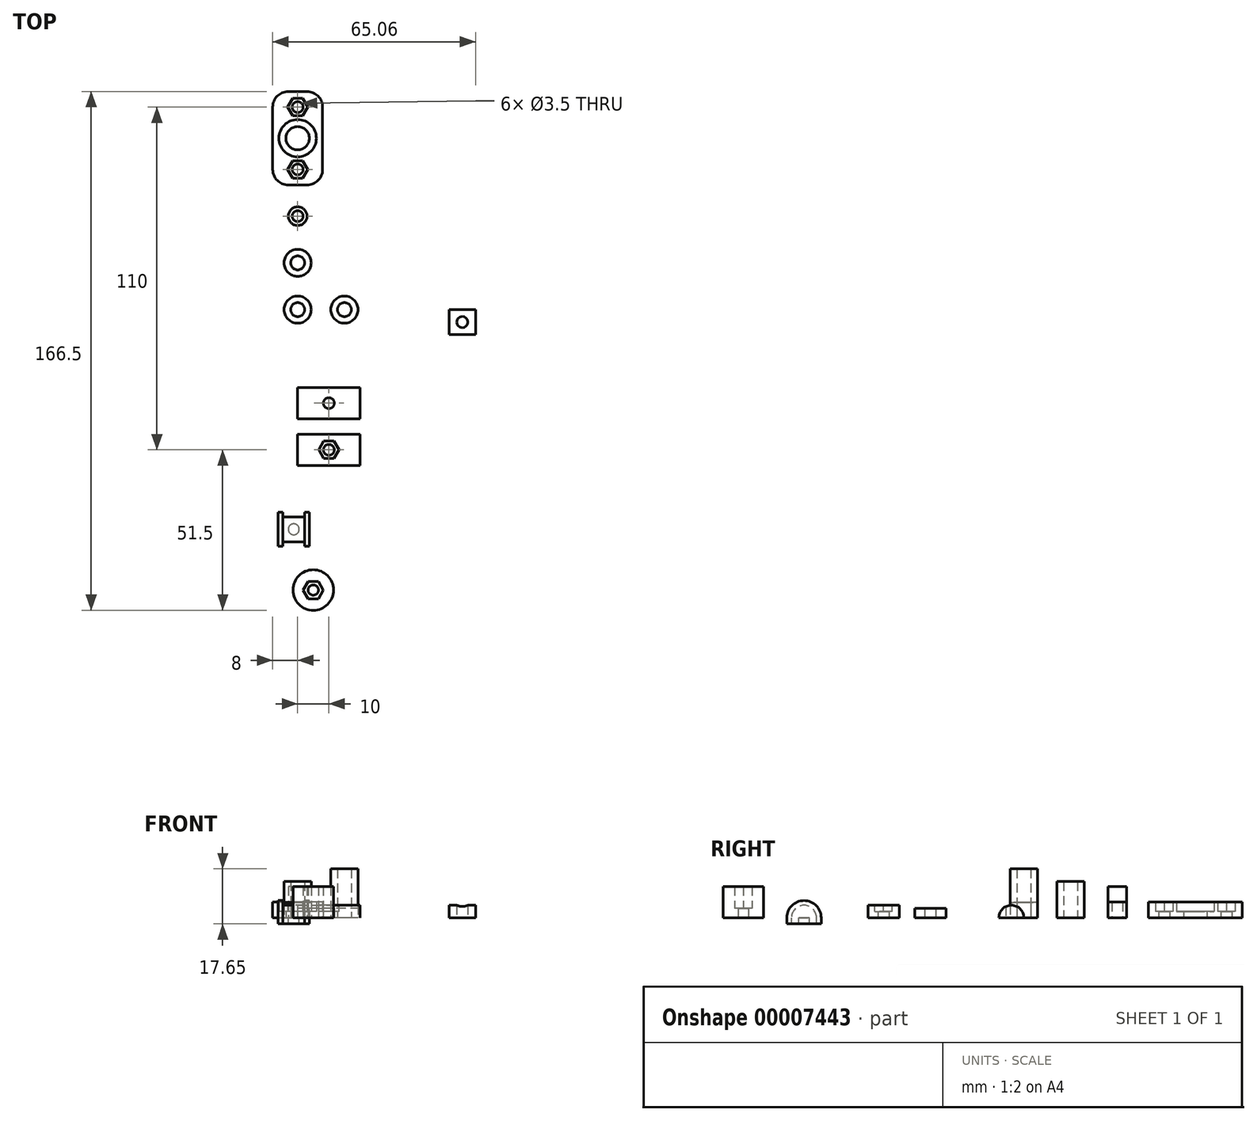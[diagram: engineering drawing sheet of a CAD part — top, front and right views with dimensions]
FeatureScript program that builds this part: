
annotation { "Feature Type Name" : "Feature", "Feature Type Description" : "" }
export const myFeature = defineFeature(function(context is Context, id is Id, definition is map)
    precondition{}
    {
        {
            var Q0;
            Q0=qCreatedBy(makeId("Top.planeOp"),FACE);
            var sketch = newSketch(context, id + "F0", { "sketchPlane" : qUnion([Q0])});
            skCircle(sketch, "E0", {"center": v(10, 30) * mm, "radius": 4.35 * mm});
            skCircle(sketch, "E1", {"center": v(10, 30) * mm, "radius": 2.25 * mm});
            skLineSegment(sketch, "E2.rect.bottom", {"start": v(30, -20) * mm, "end": v(10, -20) * mm});
            skLineSegment(sketch, "E2.rect.top", {"start": v(30, -10) * mm, "end": v(10, -10) * mm});
            skLineSegment(sketch, "E2.rect.left", {"start": v(30, -20) * mm, "end": v(30, -10) * mm});
            skLineSegment(sketch, "E2.rect.right", {"start": v(10, -20) * mm, "end": v(10, -10) * mm});
            skPoint(sketch, "E2.rect.middle", {"position": v(20, -15) * mm});
            skCircle(sketch, "E3", {"center": v(20, -15) * mm, "radius": 1.75 * mm});
            skLineSegment(sketch, "E4", {"start": v(10, -20) * mm, "end": v(10, -25) * mm, "construction": true});
            skLineSegment(sketch, "E5.rect.bottom", {"start": v(10, -25) * mm, "end": v(30, -25) * mm});
            skLineSegment(sketch, "E5.rect.top", {"start": v(10, -35) * mm, "end": v(30, -35) * mm});
            skLineSegment(sketch, "E5.rect.left", {"start": v(10, -25) * mm, "end": v(10, -35) * mm});
            skLineSegment(sketch, "E5.rect.right", {"start": v(30, -25) * mm, "end": v(30, -35) * mm});
            skPoint(sketch, "E5.rect.middle", {"position": v(20, -30) * mm});
            skLineSegment(sketch, "E6", {"start": v(30, -25) * mm, "end": v(30, -20) * mm, "construction": true});
            skCircle(sketch, "E7", {"center": v(20, -30) * mm, "radius": 1.75 * mm});
            skLineSegment(sketch, "E8", {"start": v(13.75, -55.5) * mm, "end": v(20.06, -55.5) * mm, "construction": true});
            skLineSegment(sketch, "E9", {"start": v(13.75, -55.5) * mm, "end": v(13.75, -50) * mm});
            skLineSegment(sketch, "E10", {"start": v(13.75, -50) * mm, "end": v(12.25, -50) * mm});
            skLineSegment(sketch, "E11", {"start": v(12.25, -50) * mm, "end": v(12.25, -51.5) * mm});
            skLineSegment(sketch, "E12", {"start": v(12.25, -51.5) * mm, "end": v(5.25, -51.5) * mm});
            skLineSegment(sketch, "E13", {"start": v(5.25, -51.5) * mm, "end": v(5.25, -50) * mm});
            skLineSegment(sketch, "E14", {"start": v(5.25, -50) * mm, "end": v(3.75, -50) * mm});
            skLineSegment(sketch, "E15", {"start": v(3.75, -50) * mm, "end": v(3.75, -55.5) * mm});
            skLineSegment(sketch, "E16", {"start": v(5.25, -50) * mm, "end": v(12.25, -50) * mm, "construction": true});
            skLineSegment(sketch, "E17.0.MirrorCS", {"start": v(3.75, -61) * mm, "end": v(3.75, -55.5) * mm});
            skLineSegment(sketch, "E17.1.MirrorCS", {"start": v(5.25, -61) * mm, "end": v(3.75, -61) * mm});
            skLineSegment(sketch, "E17.2.MirrorCS", {"start": v(5.25, -59.5) * mm, "end": v(5.25, -61) * mm});
            skLineSegment(sketch, "E17.3.MirrorCS", {"start": v(12.25, -59.5) * mm, "end": v(5.25, -59.5) * mm});
            skLineSegment(sketch, "E17.4.MirrorCS", {"start": v(12.25, -61) * mm, "end": v(12.25, -59.5) * mm});
            skLineSegment(sketch, "E17.5.MirrorCS", {"start": v(13.75, -55.5) * mm, "end": v(13.75, -61) * mm});
            skLineSegment(sketch, "E17.6.MirrorCS", {"start": v(13.75, -61) * mm, "end": v(12.25, -61) * mm});
            skLineSegment(sketch, "E18", {"start": v(3.75, -55.5) * mm, "end": v(13.75, -55.5) * mm});
            skCircle(sketch, "E19", {"center": v(8.75, -55.5) * mm, "radius": 1.75 * mm});
            skCircle(sketch, "E20", {"center": v(10, 15) * mm, "radius": 4.35 * mm});
            skCircle(sketch, "E21", {"center": v(10, 15) * mm, "radius": 2.25 * mm});
            skCircle(sketch, "E22", {"center": v(25, 15) * mm, "radius": 2.25 * mm});
            skCircle(sketch, "E23", {"center": v(25, 15) * mm, "radius": 4.35 * mm});
            skCircle(sketch, "E24", {"center": v(15, -75) * mm, "radius": 6.5 * mm});
            skCircle(sketch, "E25", {"center": v(15, -75) * mm, "radius": 1.65 * mm});
            skCircle(sketch, "E26.cCircle", {"center": v(15, -75) * mm, "radius": 2.8 * mm, "construction": true});
            skLineSegment(sketch, "E26.0", {"start": v(13.38, -72.2) * mm, "end": v(16.62, -72.2) * mm});
            skLineSegment(sketch, "E26.1", {"start": v(16.62, -72.2) * mm, "end": v(18.23, -75) * mm});
            skLineSegment(sketch, "E26.2", {"start": v(18.23, -75) * mm, "end": v(16.62, -77.8) * mm});
            skLineSegment(sketch, "E26.3", {"start": v(16.62, -77.8) * mm, "end": v(13.38, -77.8) * mm});
            skLineSegment(sketch, "E26.4", {"start": v(13.38, -77.8) * mm, "end": v(11.77, -75) * mm});
            skLineSegment(sketch, "E26.5", {"start": v(11.77, -75) * mm, "end": v(13.38, -72.2) * mm});
            skPoint(sketch, "E26.0.midPoint", {"position": v(15, -72.2) * mm});
            skLineSegment(sketch, "E27", {"start": v(10, 15) * mm, "end": v(25, 15) * mm, "construction": true});
            skLineSegment(sketch, "E28", {"start": v(10, 15) * mm, "end": v(10, 30) * mm, "construction": true});
            skLineSegment(sketch, "E29", {"start": v(10, 30) * mm, "end": v(10, 45) * mm, "construction": true});
            skCircle(sketch, "E30", {"center": v(10, 45) * mm, "radius": 1.75 * mm});
            skCircle(sketch, "E31", {"center": v(10, 45) * mm, "radius": 3 * mm});
            skLineSegment(sketch, "E32", {"start": v(10, 45) * mm, "end": v(10, 60) * mm, "construction": true});
            skLineSegment(sketch, "E33", {"start": v(10, 60) * mm, "end": v(10, 80) * mm, "construction": true});
            skLineSegment(sketch, "E34.rect.bottom", {"start": v(13, 55) * mm, "end": v(7, 55) * mm});
            skLineSegment(sketch, "E34.rect.top", {"start": v(13, 85) * mm, "end": v(7, 85) * mm});
            skLineSegment(sketch, "E34.rect.left", {"start": v(18, 60) * mm, "end": v(18, 80) * mm});
            skLineSegment(sketch, "E34.rect.right", {"start": v(2, 60) * mm, "end": v(2, 80) * mm});
            skPoint(sketch, "E34.rect.middle", {"position": v(10, 70) * mm});
            skCircle(sketch, "E35", {"center": v(10, 70) * mm, "radius": 3.75 * mm});
            skCircle(sketch, "E36", {"center": v(10, 60) * mm, "radius": 1.75 * mm});
            skCircle(sketch, "E37", {"center": v(10, 80) * mm, "radius": 1.75 * mm});
            skCircle(sketch, "E38.cCircle", {"center": v(10, 60) * mm, "radius": 2.8 * mm, "construction": true});
            skLineSegment(sketch, "E38.0", {"start": v(8.38, 62.8) * mm, "end": v(11.62, 62.8) * mm});
            skLineSegment(sketch, "E38.1", {"start": v(11.62, 62.8) * mm, "end": v(13.23, 60) * mm});
            skLineSegment(sketch, "E38.2", {"start": v(13.23, 60) * mm, "end": v(11.62, 57.2) * mm});
            skLineSegment(sketch, "E38.3", {"start": v(11.62, 57.2) * mm, "end": v(8.38, 57.2) * mm});
            skLineSegment(sketch, "E38.4", {"start": v(8.38, 57.2) * mm, "end": v(6.77, 60) * mm});
            skLineSegment(sketch, "E38.5", {"start": v(6.77, 60) * mm, "end": v(8.38, 62.8) * mm});
            skPoint(sketch, "E38.0.midPoint", {"position": v(10, 62.8) * mm});
            skCircle(sketch, "E39.cCircle", {"center": v(10, 80) * mm, "radius": 2.8 * mm, "construction": true});
            skLineSegment(sketch, "E39.0", {"start": v(8.38, 82.8) * mm, "end": v(11.62, 82.8) * mm});
            skLineSegment(sketch, "E39.1", {"start": v(11.62, 82.8) * mm, "end": v(13.23, 80) * mm});
            skLineSegment(sketch, "E39.2", {"start": v(13.23, 80) * mm, "end": v(11.62, 77.2) * mm});
            skLineSegment(sketch, "E39.3", {"start": v(11.62, 77.2) * mm, "end": v(8.38, 77.2) * mm});
            skLineSegment(sketch, "E39.4", {"start": v(8.38, 77.2) * mm, "end": v(6.77, 80) * mm});
            skLineSegment(sketch, "E39.5", {"start": v(6.77, 80) * mm, "end": v(8.38, 82.8) * mm});
            skPoint(sketch, "E39.0.midPoint", {"position": v(10, 82.8) * mm});
            skPoint(sketch, "E40.visualSharp", {"position": v(2, 85) * mm});
            skArc(sketch, "E40.filletArc", {"start": v(7, 85) * mm, "mid": v(3.46, 83.54) * mm, "end": v(2, 80) * mm});
            skPoint(sketch, "E41.visualSharp", {"position": v(18, 85) * mm});
            skArc(sketch, "E41.filletArc", {"start": v(18, 80) * mm, "mid": v(16.54, 83.54) * mm, "end": v(13, 85) * mm});
            skPoint(sketch, "E42.visualSharp", {"position": v(18, 55) * mm});
            skArc(sketch, "E42.filletArc", {"start": v(13, 55) * mm, "mid": v(16.54, 56.46) * mm, "end": v(18, 60) * mm});
            skPoint(sketch, "E43.visualSharp", {"position": v(2, 55) * mm});
            skArc(sketch, "E43.filletArc", {"start": v(2, 60) * mm, "mid": v(3.46, 56.46) * mm, "end": v(7, 55) * mm});
            skCircle(sketch, "E44", {"center": v(10, 70) * mm, "radius": 6 * mm});
            skSolve(sketch);
        }
        {
            var Q0;
            Q0=makeQuery(id+"F0.imprint","IMPRINT",FACE,{"disambiguationData":[TD([[makeQuery(id+"F0.imprint","IMPRINT",EDGE,{"derivedFrom":sQuery(id+"F0.wireOp",EDGE,"E0")}),1.0]])]});
            extrude(context, id + "F1", {"entities" : qUnion([Q0]), "depth" : 10 * mm + .8 * mm + .8 * mm});
        }
        {
            var Q0;
            Q0=makeQuery(id+"F0.imprint","IMPRINT",FACE,{"disambiguationData":[TD([[makeQuery(id+"F0.imprint","IMPRINT",EDGE,{"derivedFrom":sQuery(id+"F0.wireOp",EDGE,"E20")}),1.0]])]});
            extrude(context, id + "F2", {"entities" : qUnion([Q0]), "depth" : 4.6 * mm + .25 * mm});
        }
        {
            var Q0;
            Q0=makeQuery(id+"F0.imprint","IMPRINT",FACE,{"disambiguationData":[TD([[makeQuery(id+"F0.imprint","IMPRINT",EDGE,{"derivedFrom":sQuery(id+"F0.wireOp",EDGE,"E22")}),-1.0]])]});
            extrude(context, id + "F3", {"entities" : qUnion([Q0]), "depth" : 4.6 * mm + .25 * mm + 10 * mm + .8 * mm});
        }
        {
            var Q0;
            Q0=makeQuery(id+"F0.imprint","IMPRINT",FACE,{"disambiguationData":[TD([[makeQuery(id+"F0.imprint","IMPRINT",EDGE,{"derivedFrom":sQuery(id+"F0.wireOp",EDGE,"E2.rect.bottom")}),-1.0]])]});
            extrude(context, id + "F4", {"entities" : qUnion([Q0]), "depth" : 3 * mm});
        }
        {
            var Q0;
            Q0=makeQuery(id+"F0.imprint","IMPRINT",FACE,{"disambiguationData":[TD([[makeQuery(id+"F0.imprint","IMPRINT",EDGE,{"derivedFrom":sQuery(id+"F0.wireOp",EDGE,"E5.rect.bottom")}),-1.0]])]});
            extrude(context, id + "F5", {"entities" : qUnion([Q0]), "depth" : 4 * mm});
        }
        {
            var Q0;
            Q0=makeQuery(id+"F5.opExtrude","CAP_FACE",FACE,{"disambiguationData":[OSD([sQuery(id+"F0.wireOp",EDGE,"E5.rect.bottom"),sQuery(id+"F0.wireOp",EDGE,"E5.rect.top"),sQuery(id+"F0.wireOp",EDGE,"E5.rect.left"),sQuery(id+"F0.wireOp",EDGE,"E5.rect.right"),sQuery(id+"F0.wireOp",EDGE,"E7")])],"isStart":false});
            var sketch = newSketch(context, id + "F6", { "sketchPlane" : qUnion([Q0])});
            skCircle(sketch, "E45.cCircle", {"center": v(20, -30) * mm, "radius": 2.8 * mm, "construction": true});
            skLineSegment(sketch, "E45.0", {"start": v(18.38, -32.8) * mm, "end": v(16.77, -30) * mm});
            skLineSegment(sketch, "E45.1", {"start": v(16.77, -30) * mm, "end": v(18.38, -27.2) * mm});
            skLineSegment(sketch, "E45.2", {"start": v(18.38, -27.2) * mm, "end": v(21.62, -27.2) * mm});
            skLineSegment(sketch, "E45.3", {"start": v(21.62, -27.2) * mm, "end": v(23.23, -30) * mm});
            skLineSegment(sketch, "E45.4", {"start": v(23.23, -30) * mm, "end": v(21.62, -32.8) * mm});
            skLineSegment(sketch, "E45.5", {"start": v(21.62, -32.8) * mm, "end": v(18.38, -32.8) * mm});
            skPoint(sketch, "E45.0.midPoint", {"position": v(17.58, -31.4) * mm});
            skSolve(sketch);
        }
        {
            var Q0;
            Q0=makeQuery(id+"F6.imprint","IMPRINT",FACE,{"disambiguationData":[TD([[makeQuery(id+"F6.imprint","IMPRINT",EDGE,{"derivedFrom":sQuery(id+"F6.wireOp",EDGE,"E45.0")}),-1.0]])]});
            extrude(context, id + "F7", {"entities" : qUnion([Q0]), "operationType" : NewBodyOperationType.REMOVE, "oppositeDirection" : true, "depth" : 2 * mm});
        }
        {
            var Q0;
            {var subQ4=sQuery(id+"F0.wireOp",EDGE,"E9");Q0=makeQuery(id+"F0.imprint","IMPRINT",FACE,{"disambiguationData":[TD([[makeQuery(id+"F0.imprint","IMPRINT",EDGE,{"derivedFrom":subQ4}),1.0]])]});}
            var Q1;
            {var subQ5=sQuery(id+"F0.wireOp",EDGE,"E17.0.MirrorCS");Q1=makeQuery(id+"F0.imprint","IMPRINT",FACE,{"disambiguationData":[TD([[makeQuery(id+"F0.imprint","IMPRINT",EDGE,{"derivedFrom":subQ5}),-1.0]])]});}
            extrude(context, id + "F8", {"entities" : qUnion([Q0, Q1]), "oppositeDirection" : true, "depth" : 2 * mm});
        }
        {
            var Q0;
            {var subQ4=sQuery(id+"F0.wireOp",EDGE,"E9");Q0=makeQuery(id+"F0.imprint","IMPRINT",FACE,{"disambiguationData":[TD([[makeQuery(id+"F0.imprint","IMPRINT",EDGE,{"derivedFrom":subQ4}),1.0]])]});}
            var Q1;
            {var subQ0=sQuery(id+"F0.wireOp",EDGE,"E19");var subQ1=sQuery(id+"F0.wireOp",EDGE,"E18");var subQ3=makeQuery(id+"F0.imprint","INTERSECT",VERTEX,{"disambiguationData":[OD(0.0)],"derivedFrom":[subQ1,subQ0]});Q1=makeQuery(id+"F0.imprint","IMPRINT",FACE,{"disambiguationData":[TD([[makeQuery(id+"F0.imprint","IMPRINT",EDGE,{"disambiguationData":[TD([[subQ3,-1.0]])],"derivedFrom":subQ1}),1.0]])]});}
            var Q2;
            Q2=sQuery(id+"F0.wireOp",EDGE,"E8");
            revolve(context, id + "F9", {"operationType" : NewBodyOperationType.ADD, "entities" : qUnion([Q0, Q1]), "axis" : qUnion([Q2]), "revolveType" : RevolveType.ONE_DIRECTION, "angle" : 180 * degree});
        }
        {
            var Q0;
            Q0=qCreatedBy(makeId("Top.planeOp"),FACE);
            var sketch = newSketch(context, id + "F10", { "sketchPlane" : qUnion([Q0])});
            skLineSegment(sketch, "E46", {"start": v(58.56, 11) * mm, "end": v(67.06, 11) * mm});
            skLineSegment(sketch, "E47", {"start": v(67.06, 11) * mm, "end": v(67.06, 15) * mm});
            skLineSegment(sketch, "E48", {"start": v(67.06, 15) * mm, "end": v(58.56, 15) * mm});
            skLineSegment(sketch, "E49", {"start": v(58.56, 15) * mm, "end": v(58.56, 11) * mm});
            skCircle(sketch, "E50", {"center": v(62.81, 11) * mm, "radius": 1.8 * mm});
            skSolve(sketch);
        }
        {
            var Q0;
            {var subQ5=sQuery(id+"F10.wireOp",EDGE,"E47");Q0=makeQuery(id+"F10.imprint","IMPRINT",FACE,{"disambiguationData":[TD([[makeQuery(id+"F10.imprint","IMPRINT",EDGE,{"derivedFrom":subQ5}),1.0]])]});}
            var Q1;
            {var subQ0=sQuery(id+"F10.wireOp",EDGE,"E50");var subQ1=sQuery(id+"F10.wireOp",EDGE,"E46");var subQ3=makeQuery(id+"F10.imprint","INTERSECT",VERTEX,{"disambiguationData":[OD(0.0)],"derivedFrom":[subQ1,subQ0]});Q1=makeQuery(id+"F10.imprint","IMPRINT",FACE,{"disambiguationData":[TD([[makeQuery(id+"F10.imprint","IMPRINT",EDGE,{"disambiguationData":[TD([[subQ3,-1.0]])],"derivedFrom":subQ1}),1.0]])]});}
            var Q2;
            Q2=sQuery(id+"F10.wireOp",EDGE,"E46");
            revolve(context, id + "F11", {"entities" : qUnion([Q0, Q1]), "axis" : qUnion([Q2]), "revolveType" : RevolveType.ONE_DIRECTION, "angle" : 180 * degree});
        }
        {
            var Q0;
            {var subQ0=sQuery(id+"F10.wireOp",EDGE,"E50");var subQ1=sQuery(id+"F10.wireOp",EDGE,"E46");var subQ3=makeQuery(id+"F10.imprint","INTERSECT",VERTEX,{"disambiguationData":[OD(0.0)],"derivedFrom":[subQ1,subQ0]});Q0=makeQuery(id+"F10.imprint","IMPRINT",FACE,{"disambiguationData":[TD([[makeQuery(id+"F10.imprint","IMPRINT",EDGE,{"disambiguationData":[TD([[subQ3,-1.0]])],"derivedFrom":subQ1}),-1.0]])]});}
            var Q1;
            {var subQ0=sQuery(id+"F10.wireOp",EDGE,"E50");var subQ1=sQuery(id+"F10.wireOp",EDGE,"E46");var subQ3=makeQuery(id+"F10.imprint","INTERSECT",VERTEX,{"disambiguationData":[OD(0.0)],"derivedFrom":[subQ1,subQ0]});Q1=makeQuery(id+"F10.imprint","IMPRINT",FACE,{"disambiguationData":[TD([[makeQuery(id+"F10.imprint","IMPRINT",EDGE,{"disambiguationData":[TD([[subQ3,-1.0]])],"derivedFrom":subQ1}),1.0]])]});}
            extrude(context, id + "F12", {"entities" : qUnion([Q0, Q1]), "operationType" : NewBodyOperationType.REMOVE, "endBound" : BoundingType.THROUGH_ALL, "depth" : 25 * mm});
        }
        {
            var Q0;
            Q0=makeQuery(id+"F0.imprint","IMPRINT",FACE,{"disambiguationData":[TD([[makeQuery(id+"F0.imprint","IMPRINT",EDGE,{"derivedFrom":sQuery(id+"F0.wireOp",EDGE,"E24")}),1.0]])]});
            var Q1;
            Q1=makeQuery(id+"F0.imprint","IMPRINT",FACE,{"disambiguationData":[TD([[makeQuery(id+"F0.imprint","IMPRINT",EDGE,{"derivedFrom":sQuery(id+"F0.wireOp",EDGE,"E25")}),-1.0]])]});
            extrude(context, id + "F13", {"entities" : qUnion([Q0, Q1]), "depth" : 3 * mm});
        }
        {
            var Q0;
            Q0=makeQuery(id+"F0.imprint","IMPRINT",FACE,{"disambiguationData":[TD([[makeQuery(id+"F0.imprint","IMPRINT",EDGE,{"derivedFrom":sQuery(id+"F0.wireOp",EDGE,"E24")}),1.0]])]});
            extrude(context, id + "F14", {"entities" : qUnion([Q0]), "operationType" : NewBodyOperationType.ADD, "depth" : 10 * mm});
        }
        {
            var Q0;
            Q0=makeQuery(id+"F0.imprint","IMPRINT",FACE,{"disambiguationData":[TD([[makeQuery(id+"F0.imprint","IMPRINT",EDGE,{"derivedFrom":sQuery(id+"F0.wireOp",EDGE,"E30")}),-1.0]])]});
            extrude(context, id + "F15", {"entities" : qUnion([Q0]), "depth" : 10 * mm});
        }
        {
            var Q0;
            Q0=makeQuery(id+"F0.imprint","IMPRINT",FACE,{"disambiguationData":[TD([[makeQuery(id+"F0.imprint","IMPRINT",EDGE,{"derivedFrom":sQuery(id+"F0.wireOp",EDGE,"E30")}),-1.0]])]});
            extrude(context, id + "F16", {"entities" : qUnion([Q0]), "depth" : 5 * mm});
        }
        {
            var Q0;
            Q0=makeQuery(id+"F0.imprint","IMPRINT",FACE,{"disambiguationData":[TD([[makeQuery(id+"F0.imprint","IMPRINT",EDGE,{"derivedFrom":sQuery(id+"F0.wireOp",EDGE,"E34.rect.bottom")}),-1.0]])]});
            var Q1;
            Q1=makeQuery(id+"F0.imprint","IMPRINT",FACE,{"disambiguationData":[TD([[makeQuery(id+"F0.imprint","IMPRINT",EDGE,{"derivedFrom":sQuery(id+"F0.wireOp",EDGE,"E35")}),-1.0]])]});
            var Q2;
            Q2=makeQuery(id+"F0.imprint","IMPRINT",FACE,{"disambiguationData":[TD([[makeQuery(id+"F0.imprint","IMPRINT",EDGE,{"derivedFrom":sQuery(id+"F0.wireOp",EDGE,"E37")}),-1.0]])]});
            var Q3;
            Q3=makeQuery(id+"F0.imprint","IMPRINT",FACE,{"disambiguationData":[TD([[makeQuery(id+"F0.imprint","IMPRINT",EDGE,{"derivedFrom":sQuery(id+"F0.wireOp",EDGE,"E36")}),-1.0]])]});
            extrude(context, id + "F17", {"entities" : qUnion([Q0, Q1, Q2, Q3]), "depth" : 2 * mm});
        }
        {
            var Q0;
            Q0=makeQuery(id+"F0.imprint","IMPRINT",FACE,{"disambiguationData":[TD([[makeQuery(id+"F0.imprint","IMPRINT",EDGE,{"derivedFrom":sQuery(id+"F0.wireOp",EDGE,"E34.rect.bottom")}),-1.0]])]});
            extrude(context, id + "F18", {"entities" : qUnion([Q0]), "operationType" : NewBodyOperationType.ADD, "depth" : 5 * mm});
        }
    });
